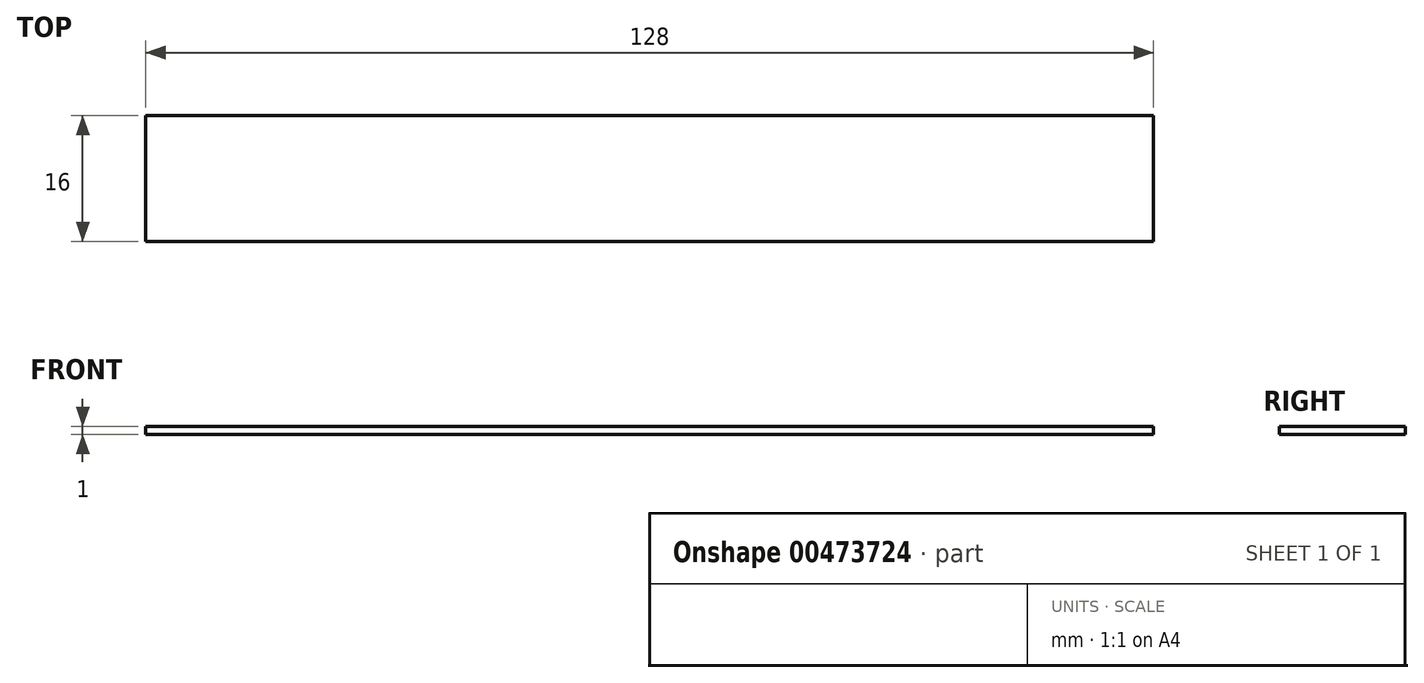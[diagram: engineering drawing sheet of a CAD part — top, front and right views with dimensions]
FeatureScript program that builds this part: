
annotation { "Feature Type Name" : "Feature", "Feature Type Description" : "" }
export const myFeature = defineFeature(function(context is Context, id is Id, definition is map)
    precondition{}
    {
        {
            var Q0;
            Q0=qCreatedBy(makeId("Top.planeOp"),FACE);
            var sketch = newSketch(context, id + "F0", { "sketchPlane" : qUnion([Q0])});
            skLineSegment(sketch, "E0.bottom", {"start": v(-62.5, -7.5) * mm, "end": v(62.5, -7.5) * mm});
            skLineSegment(sketch, "E0.top", {"start": v(-62.5, 7.5) * mm, "end": v(62.5, 7.5) * mm});
            skLineSegment(sketch, "E0.left", {"start": v(-62.5, -7.5) * mm, "end": v(-62.5, 7.5) * mm});
            skLineSegment(sketch, "E0.right", {"start": v(62.5, -7.5) * mm, "end": v(62.5, 7.5) * mm});
            skPoint(sketch, "E0.middle", {"position": v(0, 0) * mm});
            skSolve(sketch);
        }
        {
            var Q0;
            Q0 = qSketchRegion(id + "F0", true);
            extrude(context, id + "F1", {"entities" : qUnion([Q0]), "depth" : 1 * mm});
        }
        {
            var Q0;
            Q0=qCreatedBy(makeId("Top.planeOp"),FACE);
            var sketch = newSketch(context, id + "F2", { "sketchPlane" : qUnion([Q0])});
            skLineSegment(sketch, "E1.bottom", {"start": v(-64, 8) * mm, "end": v(64, 8) * mm});
            skLineSegment(sketch, "E1.top", {"start": v(-64, -8) * mm, "end": v(64, -8) * mm});
            skLineSegment(sketch, "E1.left", {"start": v(-64, 8) * mm, "end": v(-64, -8) * mm});
            skLineSegment(sketch, "E1.right", {"start": v(64, 8) * mm, "end": v(64, -8) * mm});
            skPoint(sketch, "E1.middle", {"position": v(0, 0) * mm});
            skSolve(sketch);
        }
        {
            var Q0;
            Q0 = qSketchRegion(id + "F2", true);
            extrude(context, id + "F3", {"entities" : qUnion([Q0]), "operationType" : NewBodyOperationType.ADD, "depth" : 1 * mm});
        }
    });
